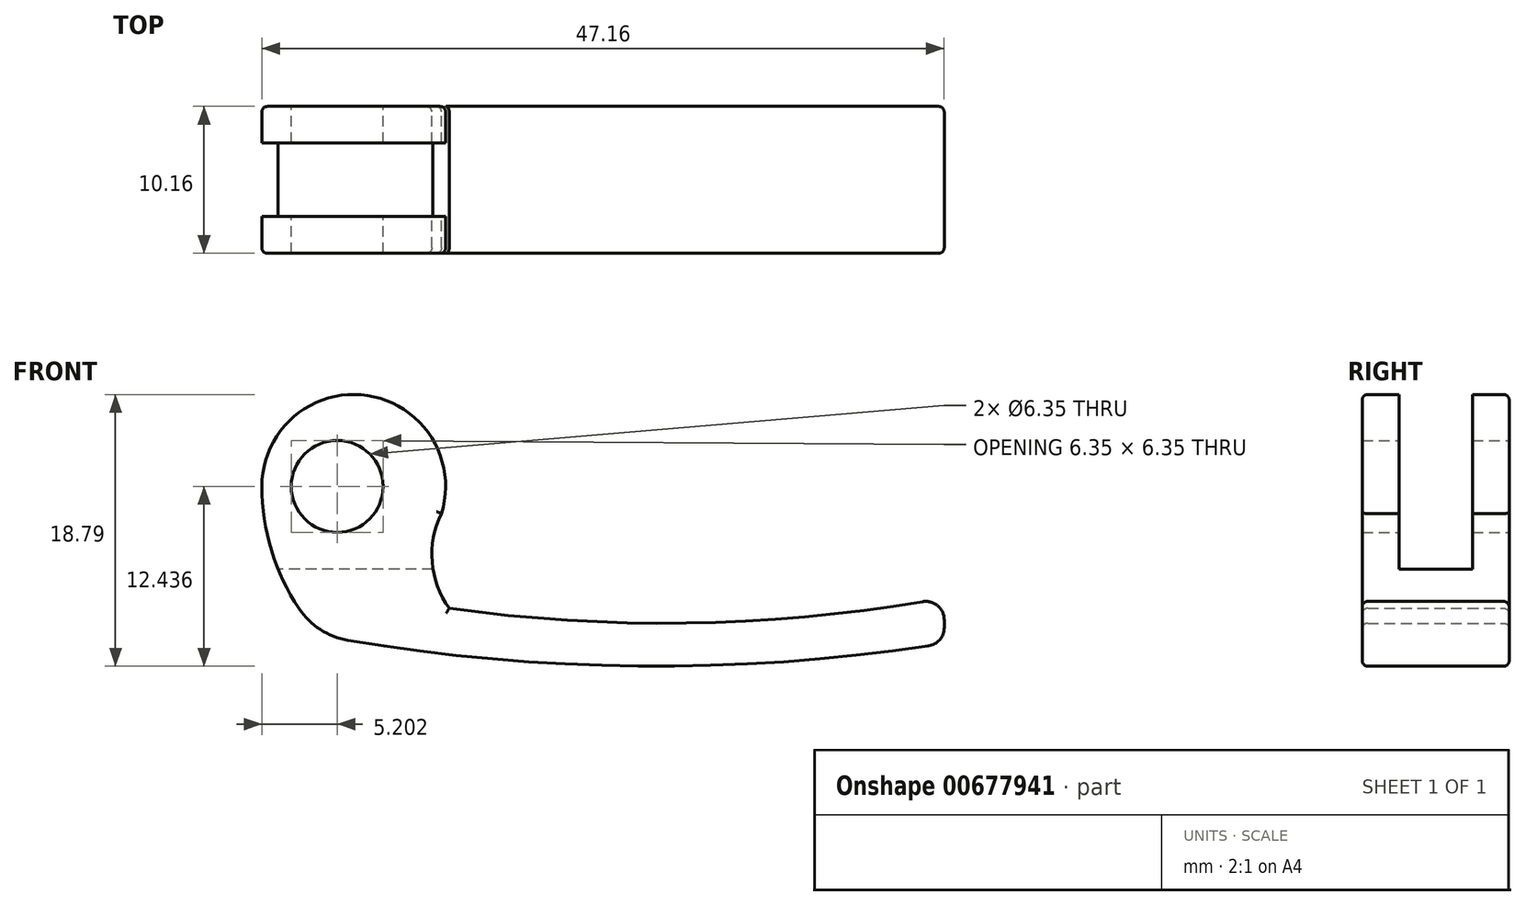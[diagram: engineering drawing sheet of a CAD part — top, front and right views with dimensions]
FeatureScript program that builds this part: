
annotation { "Feature Type Name" : "Feature", "Feature Type Description" : "" }
export const myFeature = defineFeature(function(context is Context, id is Id, definition is map)
    precondition{}
    {
        {
            var Q0;
            Q0=qCreatedBy(makeId("Front.planeOp"),FACE);
            var sketch = newSketch(context, id + "F0", { "sketchPlane" : qUnion([Q0])});
            skArc(sketch, "E0", {"start": v(-4.94, 9.62) * mm, "mid": v(-9.17, 18.63) * mm, "end": v(-16.97, 12.45) * mm});
            skLineSegment(sketch, "E1", {"start": v(-10.62, 18.8) * mm, "end": v(30.2, 18.8) * mm, "construction": true});
            skLineSegment(sketch, "E2", {"start": v(-16.97, -0.43) * mm, "end": v(30.2, -0.43) * mm, "construction": true});
            skArc(sketch, "E3", {"start": v(-4.56, 10.56) * mm, "mid": v(-5.2, 7.21) * mm, "end": v(-4.03, 4.02) * mm});
            skLineSegment(sketch, "E4", {"start": v(30.2, 0) * mm, "end": v(-16.97, 0) * mm, "construction": true});
            skLineSegment(sketch, "E5", {"start": v(-16.97, 12.45) * mm, "end": v(-16.97, -0.43) * mm, "construction": true});
            skLineSegment(sketch, "E6", {"start": v(30.2, 18.8) * mm, "end": v(30.2, -0.43) * mm, "construction": true});
            skPoint(sketch, "E7.orphan", {"position": v(35.32, 0) * mm});
            skPoint(sketch, "E8.orphan", {"position": v(35.32, -0.43) * mm});
            skPoint(sketch, "E9.orphan", {"position": v(-10.62, -0.43) * mm});
            skArc(sketch, "E10", {"start": v(-4.03, 4.02) * mm, "mid": v(13.11, 3) * mm, "end": v(30.2, 4.73) * mm});
            skArc(sketch, "E11", {"start": v(-12.95, 2.15) * mm, "mid": v(8.6, 0.03) * mm, "end": v(30.2, 1.58) * mm});
            skArc(sketch, "E12", {"start": v(-16.97, 12.45) * mm, "mid": v(-15.93, 6.92) * mm, "end": v(-12.95, 2.15) * mm});
            skCircle(sketch, "E13", {"center": v(-11.77, 12.45) * mm, "radius": 3.18 * mm});
            skLineSegment(sketch, "E14", {"start": v(30.2, 4.73) * mm, "end": v(30.2, 1.58) * mm});
            skSolve(sketch);
        }
        {
            var Q0;
            {var subQ0=sQuery(id+"F0.wireOp",EDGE,"E10");Q0=makeQuery(id+"F0.imprint","IMPRINT",FACE,{"disambiguationData":[TD([[makeQuery(id+"F0.imprint","IMPRINT",EDGE,{"derivedFrom":subQ0}),-1.0]])]});}
            extrude(context, id + "F1", {"entities" : qUnion([Q0]), "depth" : 10.16 * mm, "offsetDistance" : 25.4 * mm});
        }
        {
            var Q0;
            Q0=makeQuery(id+"F1.opExtrude","CAP_EDGE",EDGE,{"disambiguationData":[OSD([sQuery(id+"F0.wireOp",EDGE,"E0")])],"isStart":false});
            var Q1;
            Q1=makeQuery(id+"F1.opExtrude","CAP_EDGE",EDGE,{"disambiguationData":[OSD([sQuery(id+"F0.wireOp",EDGE,"E3")])],"isStart":false});
            var Q2;
            Q2=makeQuery(id+"F1.opExtrude","CAP_EDGE",EDGE,{"disambiguationData":[OSD([sQuery(id+"F0.wireOp",EDGE,"E10")])],"isStart":false});
            var Q3;
            Q3=makeQuery(id+"F1.opExtrude","CAP_EDGE",EDGE,{"disambiguationData":[OSD([sQuery(id+"F0.wireOp",EDGE,"E14")])],"isStart":false});
            var Q4;
            Q4=makeQuery(id+"F1.opExtrude","CAP_EDGE",EDGE,{"disambiguationData":[OSD([sQuery(id+"F0.wireOp",EDGE,"E11")])],"isStart":false});
            var Q5;
            Q5=makeQuery(id+"F1.opExtrude","CAP_EDGE",EDGE,{"disambiguationData":[OSD([sQuery(id+"F0.wireOp",EDGE,"E12")])],"isStart":false});
            var Q6;
            Q6=makeQuery(id+"F1.opExtrude","CAP_EDGE",EDGE,{"disambiguationData":[OSD([sQuery(id+"F0.wireOp",EDGE,"E0")])],"isStart":true});
            var Q7;
            Q7=makeQuery(id+"F1.opExtrude","CAP_EDGE",EDGE,{"disambiguationData":[OSD([sQuery(id+"F0.wireOp",EDGE,"E12")])],"isStart":true});
            var Q8;
            Q8=makeQuery(id+"F1.opExtrude","CAP_EDGE",EDGE,{"disambiguationData":[OSD([sQuery(id+"F0.wireOp",EDGE,"E3")])],"isStart":true});
            var Q9;
            Q9=makeQuery(id+"F1.opExtrude","CAP_EDGE",EDGE,{"disambiguationData":[OSD([sQuery(id+"F0.wireOp",EDGE,"E10")])],"isStart":true});
            var Q10;
            Q10=makeQuery(id+"F1.opExtrude","CAP_EDGE",EDGE,{"disambiguationData":[OSD([sQuery(id+"F0.wireOp",EDGE,"E11")])],"isStart":true});
            var Q11;
            Q11=makeQuery(id+"F1.opExtrude","CAP_EDGE",EDGE,{"disambiguationData":[OSD([sQuery(id+"F0.wireOp",EDGE,"E14")])],"isStart":true});
            fillet(context, id + "F2", {"entities" : qUnion([Q0, Q1, Q2, Q3, Q4, Q5, Q6, Q7, Q8, Q9, Q10, Q11]), "radius" : 0.38 * mm, "tangentPropagation" : true, "allowEdgeOverflow" : false});
        }
        {
            var Q0;
            Q0=makeQuery(id+"F1.opExtrude","SWEPT_EDGE",EDGE,{"disambiguationData":[OSD([sQuery(id+"F0.wireOp",EDGE,"E11"),sQuery(id+"F0.wireOp",EDGE,"E12")])]});
            fillet(context, id + "F3", {"entities" : qUnion([Q0]), "radius" : 5.08 * mm, "tangentPropagation" : true, "allowEdgeOverflow" : false});
        }
        {
            var Q0;
            Q0=makeQuery(id+"F1.opExtrude","SWEPT_EDGE",EDGE,{"disambiguationData":[OSD([sQuery(id+"F0.wireOp",EDGE,"E10"),sQuery(id+"F0.wireOp",EDGE,"E14")])]});
            var Q1;
            Q1=makeQuery(id+"F1.opExtrude","SWEPT_EDGE",EDGE,{"disambiguationData":[OSD([sQuery(id+"F0.wireOp",EDGE,"E11"),sQuery(id+"F0.wireOp",EDGE,"E14")])]});
            fillet(context, id + "F4", {"entities" : qUnion([Q0, Q1]), "radius" : 1.27 * mm, "tangentPropagation" : true, "allowEdgeOverflow" : false});
        }
        {
            var Q0;
            Q0=qCreatedBy(makeId("Right.planeOp"),FACE);
            cPlane(context, id + "F5", {"entities" : qUnion([Q0]), "cplaneType" : CPlaneType.OFFSET, "offset" : 16.97 * mm, "oppositeDirection" : true, "width" : 152.4 * mm, "height" : 152.4 * mm});
        }
        {
            var Q0;
            Q0=qCreatedBy(id+"F5.planeOp",FACE);
            var sketch = newSketch(context, id + "F6", { "sketchPlane" : qUnion([Q0])});
            skLineSegment(sketch, "E15.bottom", {"start": v(-2.54, 18.8) * mm, "end": v(-7.62, 18.8) * mm});
            skLineSegment(sketch, "E15.top", {"start": v(-2.54, 6.73) * mm, "end": v(-7.62, 6.73) * mm});
            skLineSegment(sketch, "E15.left", {"start": v(-2.54, 18.8) * mm, "end": v(-2.54, 6.73) * mm});
            skLineSegment(sketch, "E15.right", {"start": v(-7.62, 18.8) * mm, "end": v(-7.62, 6.73) * mm});
            skSolve(sketch);
        }
        {
            var Q0;
            Q0=makeQuery(id+"F6.imprint","IMPRINT",FACE,{"disambiguationData":[TD([[makeQuery(id+"F6.imprint","IMPRINT",EDGE,{"derivedFrom":sQuery(id+"F6.wireOp",EDGE,"E15.bottom")}),1.0]])]});
            extrude(context, id + "F7", {"entities" : qUnion([Q0]), "operationType" : NewBodyOperationType.REMOVE, "depth" : 15.24 * mm, "offsetDistance" : 25.4 * mm});
        }
    });
